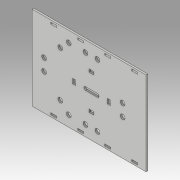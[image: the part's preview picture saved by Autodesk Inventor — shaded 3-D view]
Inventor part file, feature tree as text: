
AUTODESK INVENTOR PART (.ipt)
format: ipt  version: 2019.3 (Build 233278000, 278)  size: 196,096 bytes
history: native  units: mm
features: extrude x1, sketch x1
ambient origin geometry x8: Origin, YZ Plane, XZ Plane, XY Plane, X Axis, Y Axis, Z Axis, Center Point
bodies: Body1 (feature_tree)
feature tree (2):
  extrude  "Extrusion5"  Depth=140.0mm
  sketch  "Sketch1"  dims[d3=8.0mm d5=140.0mm d6=190.0mm d7=80.0mm d8=52.0mm d9=80.0mm d10=52.0mm d11=27.0mm d12=30.0mm d13=10.0mm d14=10.0mm d15=10.0mm d16=10.0mm d17=12.0mm d18=12.0mm d19=12.0mm d20=12.0mm d21=10.0mm d35=10.0mm d36=3.0mm d38=45.0mm d39=45.0mm d40=45.0mm d41=24.0mm d42=3.0mm d43=3.0mm d46=5.5mm d47=20.0mm d54=73.987803mm d60=5.0mm d61=29.0mm d62=29.0mm d63=8.0mm d66=8.0mm d67=29.0mm d68=29.0mm d69=3.0mm d70=0.0mm]
